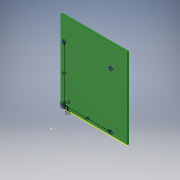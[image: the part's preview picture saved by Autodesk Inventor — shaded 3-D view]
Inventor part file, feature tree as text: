
AUTODESK INVENTOR PART (.ipt)
format: ipt  version: 2019.4 (Build 234330000, 330)  size: 103,936 bytes
history: native  units: mm
features: sketch x1, imported_body x1
ambient origin geometry x8: Origin, YZ Plane, XZ Plane, XY Plane, X Axis, Y Axis, Z Axis, Center Point
bodies: Solid1 (feature_tree)
feature tree (2):
  sketch  "Sketch1"  dims[d0=3.5mm d1=3.5mm d2=3.5mm d3=20.0mm d5=49.0mm d6=20.0mm d8=58.0mm]
  imported_body  "Base1"
